# Revit family: QF_ELECTROLUXPROFESSIONAL_1LSNTH_WS6-35_S
name_source: partatom
category: Attrezzature speciali
units: mm (PartAtom-declared; Revit-internal decimal feet)

## family parameters
Basato su piano di lavoro = No
Condiviso = No
Punto di calcolo locali = No
Quota connettore circolare = Usa diametro
Sempre verticale = Sì
Taglio con vuoti quando caricato = No
Tipo di parte = Normale

## types (3) — shared parameters
Cycle = 50 Hz
Depth = 1115.4 mm  [stored 3.65945 ft]
Depth Actual = 1115 mm  [stored 3.65814 ft]
Height = 1466.8 mm  [stored 4.81234 ft]
Height Actual = 1465 mm  [stored 4.80643 ft]
Latent Heat Output = 0.0
Length Actual = 910 mm
Modello = WS6-35
Phase = 1
Produttore = Electrolux Professional
Sensible Heat Output = 0.0
URL = www.electroluxprofessional.com
Volts = 240 V
Watts = 1300 W
Weight = 307
Width = 910 mm
zero-valued in all types: Gas KW, Prospetto di default, Steam Pounds per Hour

## per-type parameters (varying)
| type | Descrizione | Item Number |
| 9868130332 | WASHER WS6-35 35KG STEAM 220-240/50/1N COMPASS PRO 6G01 ML 2xWATER POWDER+5xLIQ. EL.VALV.OPEN SST/SILVER 2.I/O DISCON. S | 1L0H91 |
| 9868130177 | WASHER WS6-35 35KG STEAM 220-240/50/1N COMPASS PRO 6G01 ML 2xWATER POWDER VALV.OPEN SILVER DISCON. STOP | 1L0GCG |
| 9868130369 | WASHER WS6-35 35KG STEAM 220-240/50/1N COMPASS PRO 6G01 ML 2xWATER POWDER+5xLIQ. VALV.OPEN SST/SILVER 2.I/O DISCON. STOP | 1L0HJC |

note: [stored X ft] marks values corroborated as IEEE doubles in the binary element streams (Revit-internal decimal feet)

## geometry (parser evidence)
native form markers: Sweep x4
no freeform markers — native parametric forms only
